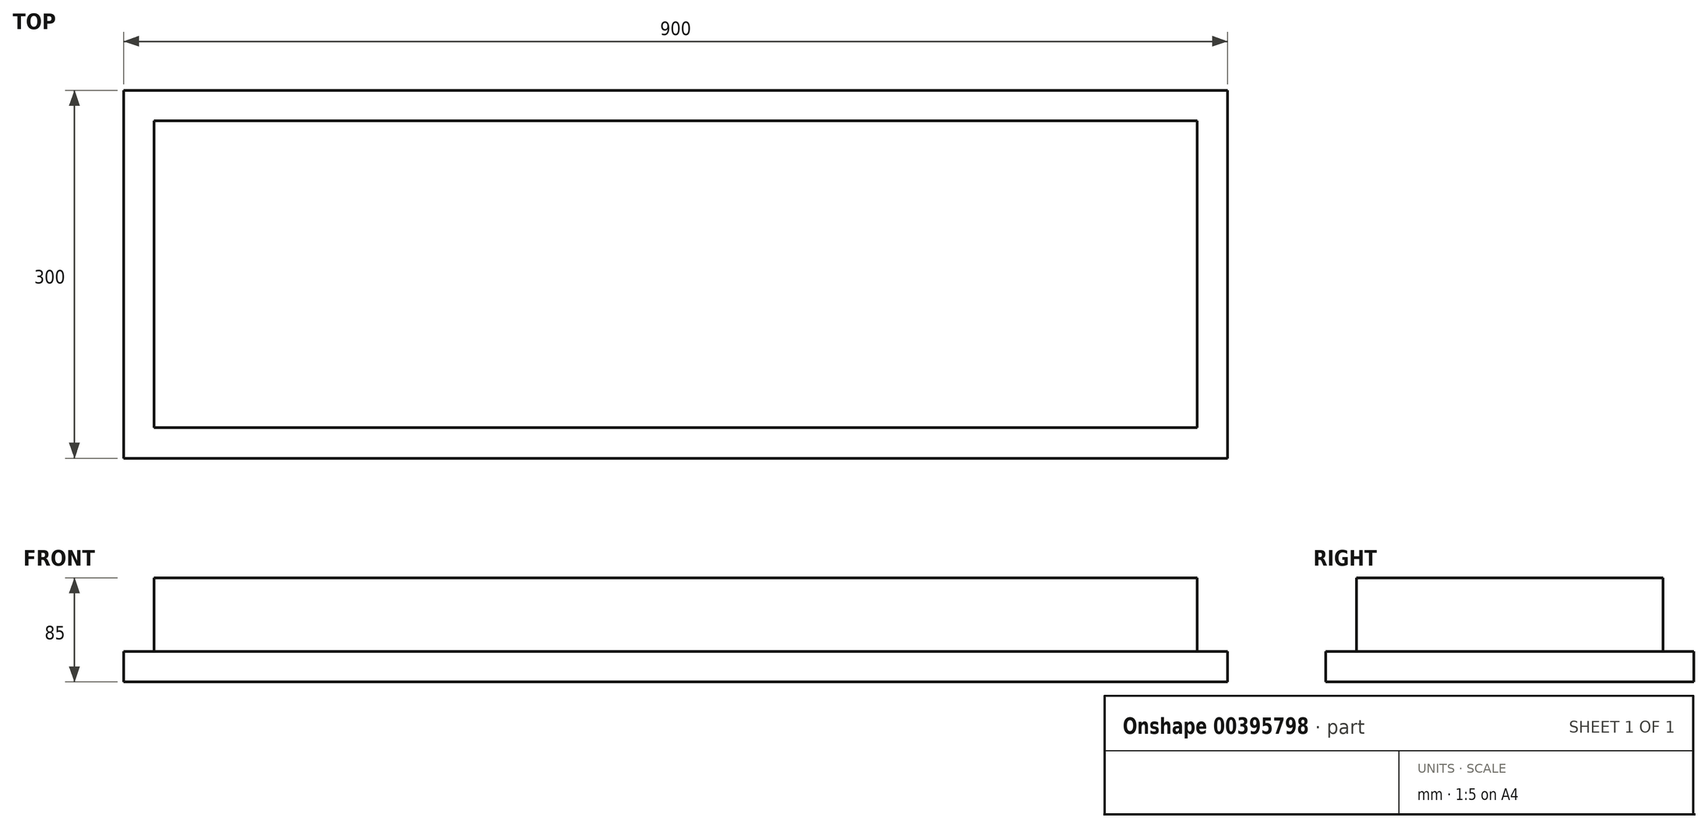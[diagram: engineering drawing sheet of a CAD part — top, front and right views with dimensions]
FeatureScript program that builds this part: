
annotation { "Feature Type Name" : "Feature", "Feature Type Description" : "" }
export const myFeature = defineFeature(function(context is Context, id is Id, definition is map)
    precondition{}
    {
        {
            var Q0;
            Q0=qCreatedBy(makeId("Top.planeOp"),FACE);
            var sketch = newSketch(context, id + "F0", { "sketchPlane" : qUnion([Q0])});
            skLineSegment(sketch, "E0.bottom", {"start": v(-450, -150) * mm, "end": v(450, -150) * mm});
            skLineSegment(sketch, "E0.top", {"start": v(-450, 150) * mm, "end": v(450, 150) * mm});
            skLineSegment(sketch, "E0.left", {"start": v(-450, -150) * mm, "end": v(-450, 150) * mm});
            skLineSegment(sketch, "E0.right", {"start": v(450, -150) * mm, "end": v(450, 150) * mm});
            skPoint(sketch, "E0.middle", {"position": v(0, 0) * mm});
            skSolve(sketch);
        }
        {
            var Q0;
            Q0=makeQuery(id+"F0.imprint","IMPRINT",FACE,{"disambiguationData":[TD([[makeQuery(id+"F0.imprint","IMPRINT",EDGE,{"derivedFrom":sQuery(id+"F0.wireOp",EDGE,"E0.bottom")}),1.0]])]});
            extrude(context, id + "F1", {"entities" : qUnion([Q0]), "depth" : 25 * mm});
        }
        {
            var Q0;
            Q0=makeQuery(id+"F1.opExtrude","CAP_FACE",FACE,{"disambiguationData":[OSD([sQuery(id+"F0.wireOp",EDGE,"E0.bottom"),sQuery(id+"F0.wireOp",EDGE,"E0.top"),sQuery(id+"F0.wireOp",EDGE,"E0.left"),sQuery(id+"F0.wireOp",EDGE,"E0.right")])],"isStart":false});
            var sketch = newSketch(context, id + "F2", { "sketchPlane" : qUnion([Q0])});
            skLineSegment(sketch, "E1.bottom", {"start": v(-425, -125) * mm, "end": v(425, -125) * mm});
            skLineSegment(sketch, "E1.top", {"start": v(-425, 125) * mm, "end": v(425, 125) * mm});
            skLineSegment(sketch, "E1.left", {"start": v(-425, -125) * mm, "end": v(-425, 125) * mm});
            skLineSegment(sketch, "E1.right", {"start": v(425, -125) * mm, "end": v(425, 125) * mm});
            skPoint(sketch, "E1.middle", {"position": v(0, 0) * mm});
            skSolve(sketch);
        }
        {
            var Q0;
            Q0=makeQuery(id+"F2.imprint","IMPRINT",FACE,{"disambiguationData":[TD([[makeQuery(id+"F2.imprint","IMPRINT",EDGE,{"derivedFrom":sQuery(id+"F2.wireOp",EDGE,"E1.bottom")}),1.0]])]});
            extrude(context, id + "F3", {"entities" : qUnion([Q0]), "operationType" : NewBodyOperationType.ADD, "depth" : 60 * mm});
        }
        {
            var Q0;
            Q0=makeQuery(id+"F3.opExtrude","SWEPT_EDGE",EDGE,{"disambiguationData":[OSD([sQuery(id+"F2.wireOp",EDGE,"E1.bottom"),sQuery(id+"F2.wireOp",EDGE,"E1.left")])]});
            cPlane(context, id + "F4", {"entities" : qUnion([Q0]), "cplaneType" : CPlaneType.MID_PLANE, "offset" : 25 * mm, "width" : 150 * mm, "height" : 150 * mm});
        }
    });
